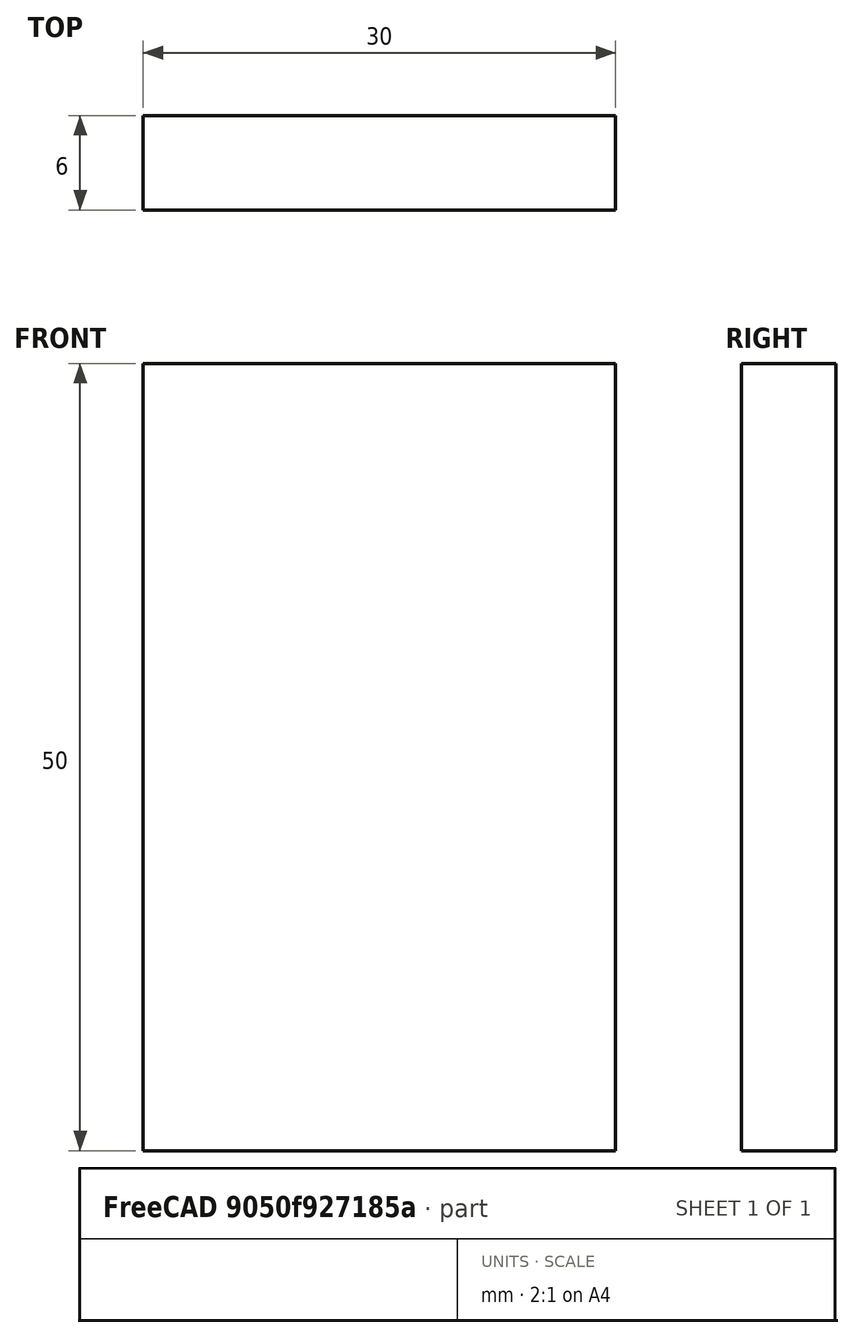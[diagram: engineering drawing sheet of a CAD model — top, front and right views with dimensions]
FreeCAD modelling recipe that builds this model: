
FCSTD DOCUMENT  (FreeCAD 0.15R4671 (Git))
Label: Flat Bar 30x6 EN10058 S235JR
License: All rights reserved
LicenseURL: http://en.wikipedia.org/wiki/All_rights_reserved
objects: Sketcher::SketchObject×1, Part::Extrusion×1
note: 2 computed .brp shape members not serialized (recipe doc carries the construction recipe); baked Part::Feature solids carry a one-line shape summary decoded from their .brp

FEATURE [Sketcher::SketchObject] Sketch
  sketch-geometry (4):
    g0: LineSegment StartX=-15 StartY=-3 StartZ=0 EndX=15 EndY=-3 EndZ=0
    g1: LineSegment StartX=15 StartY=-3 StartZ=0 EndX=15 EndY=3 EndZ=0
    g2: LineSegment StartX=15 StartY=3 StartZ=0 EndX=-15 EndY=3 EndZ=0
    g3: LineSegment StartX=-15 StartY=3 StartZ=0 EndX=-15 EndY=-3 EndZ=0
  constraints (12):
    c: Coincident(g0,g1)
    c: Coincident(g1,g2)
    c: Coincident(g2,g3)
    c: Coincident(g3,g0)
    c: Horizontal(g0)
    c: Horizontal(g2)
    c: Vertical(g1)
    c: Vertical(g3)
    c: Symmetric(g1,g2,g-2)
    c: Symmetric(g0,g1,g-1)
    c: DistanceY(g1) = 6
    c: DistanceX(g0) = 30
FEATURE [Part::Extrusion] Extrude  label="Flat Bar 30x6 EN10058 S235JR"
  Base = -> Sketch
  Dir = (0,0,50)
  Solid = true
